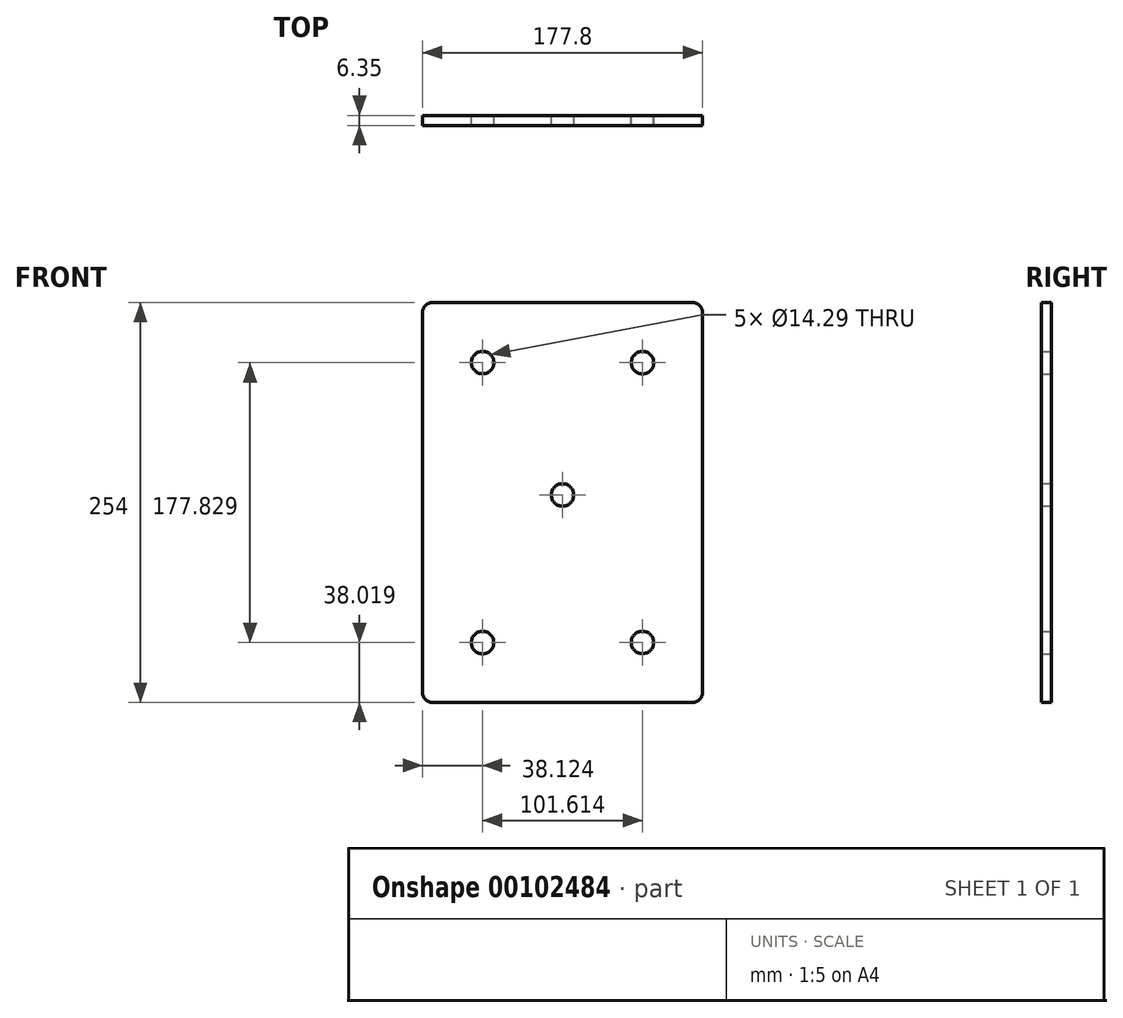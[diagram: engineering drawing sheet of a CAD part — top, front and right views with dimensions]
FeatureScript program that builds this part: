
annotation { "Feature Type Name" : "Feature", "Feature Type Description" : "" }
export const myFeature = defineFeature(function(context is Context, id is Id, definition is map)
    precondition{}
    {
        {
            var Q0;
            Q0=qCreatedBy(makeId("Front.planeOp"),FACE);
            var sketch = newSketch(context, id + "F0", { "sketchPlane" : qUnion([Q0])});
            skLineSegment(sketch, "E0", {"start": v(82.55, 127) * mm, "end": v(-82.55, 127) * mm});
            skArc(sketch, "E1", {"start": v(-82.55, 127) * mm, "mid": v(-87.04, 125.14) * mm, "end": v(-88.9, 120.65) * mm});
            skLineSegment(sketch, "E2", {"start": v(-88.9, 120.65) * mm, "end": v(-88.9, -120.65) * mm});
            skArc(sketch, "E3", {"start": v(-88.9, -120.65) * mm, "mid": v(-87.04, -125.14) * mm, "end": v(-82.55, -127) * mm});
            skLineSegment(sketch, "E4", {"start": v(-82.55, -127) * mm, "end": v(82.55, -127) * mm});
            skArc(sketch, "E5", {"start": v(82.55, -127) * mm, "mid": v(87.04, -125.14) * mm, "end": v(88.9, -120.65) * mm});
            skLineSegment(sketch, "E6", {"start": v(88.9, -120.65) * mm, "end": v(88.9, 120.65) * mm});
            skArc(sketch, "E7", {"start": v(88.9, 120.65) * mm, "mid": v(87.04, 125.14) * mm, "end": v(82.55, 127) * mm});
            skCircle(sketch, "E8", {"center": v(-50.74, 88.85) * mm, "radius": 7.14 * mm});
            skCircle(sketch, "E9", {"center": v(-50.78, -88.98) * mm, "radius": 7.14 * mm});
            skCircle(sketch, "E10", {"center": v(50.78, -88.92) * mm, "radius": 7.14 * mm});
            skCircle(sketch, "E11", {"center": v(0, 4.76) * mm, "radius": 7.14 * mm});
            skCircle(sketch, "E12", {"center": v(50.84, 88.8) * mm, "radius": 7.14 * mm});
            skSolve(sketch);
        }
        {
            var Q0;
            Q0 = qSketchRegion(id + "F0", true);
            extrude(context, id + "F1", {"entities" : qUnion([Q0]), "depth" : 6.35 * mm});
        }
    });
